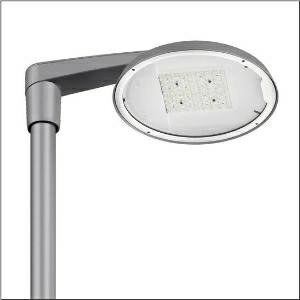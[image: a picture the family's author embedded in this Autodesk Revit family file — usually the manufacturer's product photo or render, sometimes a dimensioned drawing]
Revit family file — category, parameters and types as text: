
# Revit family: dl_r__50_iq_mini___st0_5a_5xa248b31f08ne_6eba
name_source: partatom
category: Lighting Fixtures
units: mm (PartAtom-declared; Revit-internal decimal feet)

## family parameters
Cut with Voids When Loaded = No
Host = Face
Light Source = No
Part Type = Normal
Room Calculation Point = No
Round Connector Dimension = Use Diameter
Shared = No

## types (1)
- --- (1 x LED, 19270 lm, 121.8 W, 3000K)
    Apparent Load = 122 VA
    CIE Flux Codes = 43 76 97 100 100
    Color Rendering = 70
    Color Temperature = 3000K
    Default Elevation = 1800 mm
    Description = DL® 50 iQ mini, mast luminaire, primary light control with lens, of PMMA, primary optical cover: cover, of toughened safety glass, transparent, light distribution: ST0.5a, light emission: direct distribution, primary light characteristic: asymmetric, installation type: side-entry, post-top, LED, High Power LED, rated luminous flux: 19.270lm, luminous efficacy: 158lm/W, light colour: 730, colour temperature: 3000K, control gear: iQ Street-Remote, control: optimised constant luminous flux control (CLO 2.0), Desk-Remote (wireless, voltage-free reading and setting of iQ features in the workshop via application-optimized NFC function/RFID function), Light-Fading, Smart-Wire, Night-Set, Lumen-Switch, Temp-Guard, Auto-Match, Street-Remote, mains connection: 230..240V, AC, 50/60Hz, connection cable pre-assembled, cable length: 10,5m, start of lifetime: 122W, end of service life: 134W, reduction: 55W, luminaire housing, of diecast aluminium, powder-coated, Siteco® metallic grey (DB 702S), inclination adjustable: 0°, 5°, 10° (post-top) | 0°, -5°, -10°, -15° (side-entry), please order mast post-top element or mast side-entry element separately, diameter: 500mm, height: 115mm, post-top: for spigot size d x l = 76 x 100mm; with reducer (optional accessory) 60 x 100mm | side-entry: for spigot size d x l = 60 x 100mm; with reducer (optional accessory) 42 x 100mm, mounting height: 4..6m, protection rating (complete): IP66, insulation class (complete): insulation class II (safety insulation), certification: CE, ENEC, ENEC+, VDE, impact resistance: IK08, permissible operating ambient temperature for outdoor applications: -25..+40°C, standard-compliant lighting for roads and squares, packaging unit: 1 piece

Light Distribution: ST0.5a
    Height = 115 mm
    Lamp = 1 x LED
    Lamp Light Flux = 19270 lm
    Lamp Power = 121.8 W
    Lamp count = 1
    Length = 500 mm
    Luminous efficacy = 158 lm/W
    Manufacturer = Siteco
    ModVariant = No
    Model = 5XA248B31F08NE
    Number of Poles = 1
    OnlyDefault = Yes
    Power Factor = 1
    Product Name = DL® 50 iQ mini | ST0.5a
    Product group = mast luminaire | pylon top
    ProductGroupID = 6100
    Protection Class = Protection class II
    Protection Degree = IP 66
    RLX_Detail_Level = 1
    RLX_Emergency_Light_Flux = 0 lm
    RLX_Emergency_Type = 0
    RLX_Emergency_Type_DB = No
    RlxData = <blob elided: 128261 chars, md5=d6e6dc85>
    Socket = socket
    Standby Power = 0 W
    System Light Flux = 19270 lm
    System Power = 122 W
    Type Comments = factory setting: luminous flux: 100 % | dim-lin: 254 | 657 mA
    Type Image = l_1251790.jpg
    URL = http://relux.com
    VarID = @adj_142844
    Voltage = 0 V
    Weight = 0.00 kg
    Width = 0 mm  [stored 0 ft]

note: [stored X ft] marks values corroborated as IEEE doubles in the binary element streams (Revit-internal decimal feet)

## geometry (parser evidence)
native form markers: Blend x4, Sweep x10
no freeform markers — native parametric forms only
